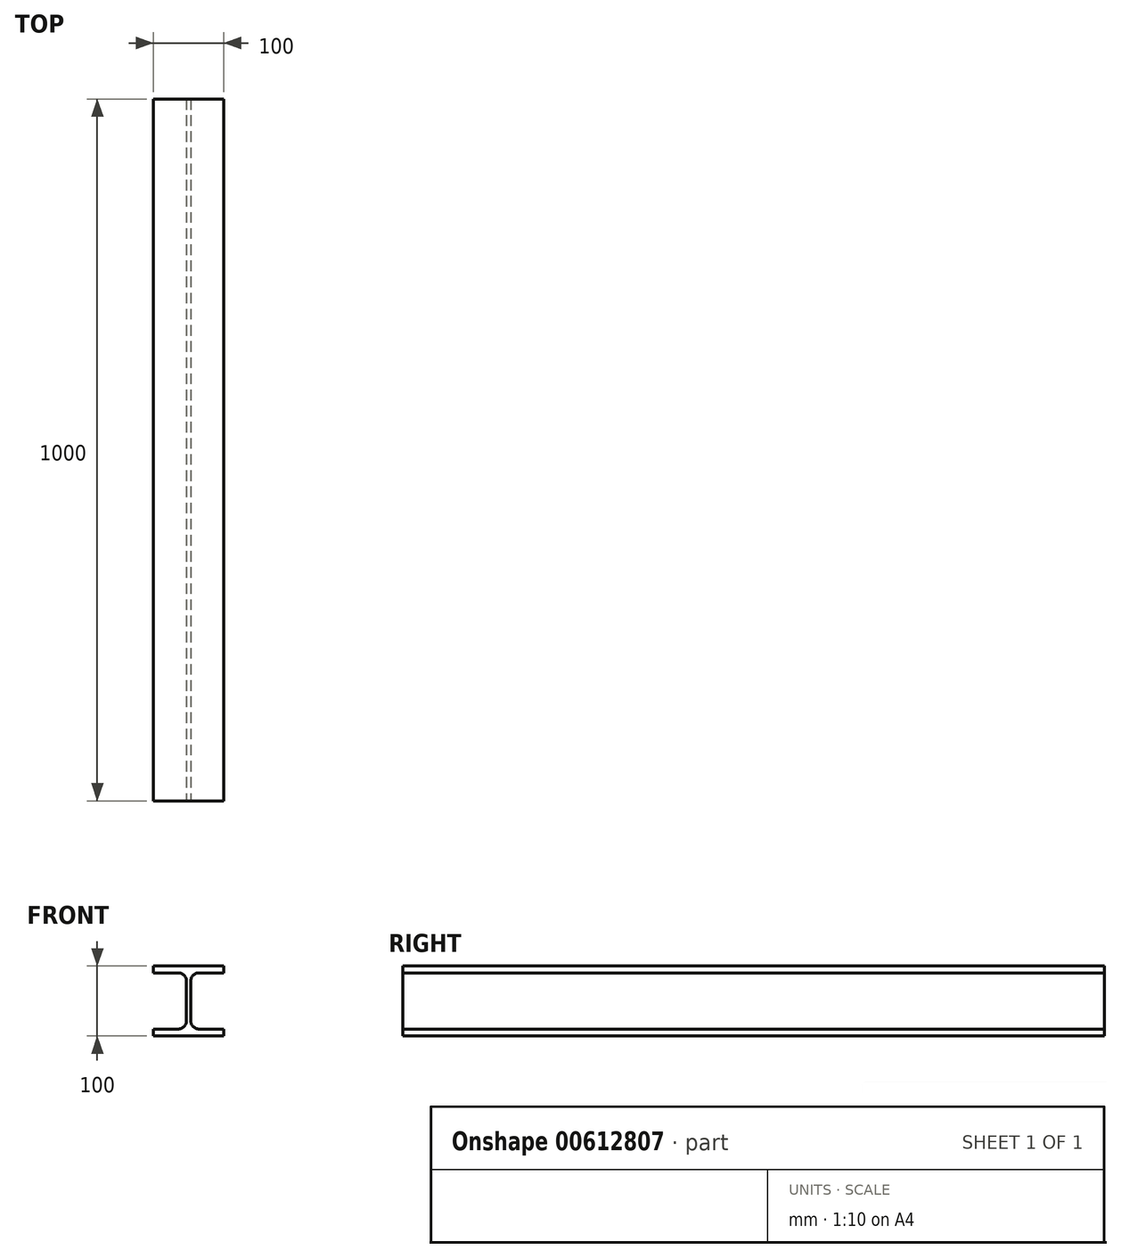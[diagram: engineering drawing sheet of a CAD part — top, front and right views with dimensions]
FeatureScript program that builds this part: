
annotation { "Feature Type Name" : "Feature", "Feature Type Description" : "" }
export const myFeature = defineFeature(function(context is Context, id is Id, definition is map)
    precondition{}
    {
        {
            var Q0;
            Q0=qCreatedBy(makeId("Front.planeOp"),FACE);
            var sketch = newSketch(context, id + "F0", { "sketchPlane" : qUnion([Q0])});
            skLineSegment(sketch, "E0.left", {"start": v(50, -40) * mm, "end": v(50, -50) * mm});
            skPoint(sketch, "E0.middle", {"position": v(0, 0) * mm});
            skLineSegment(sketch, "E1", {"start": v(3, 0) * mm, "end": v(3, -28) * mm});
            skLineSegment(sketch, "E2", {"start": v(50, -40) * mm, "end": v(15, -40) * mm});
            skPoint(sketch, "E3.newPointB", {"position": v(0, -40) * mm});
            skArc(sketch, "E3.filletArc", {"start": v(3, -28) * mm, "mid": v(6.51, -36.49) * mm, "end": v(15, -40) * mm});
            skPoint(sketch, "E0.bottom.start.orphan", {"position": v(50, 50) * mm});
            skPoint(sketch, "E0.right.start.orphan", {"position": v(-50, 50) * mm});
            skPoint(sketch, "E0.top.end.orphan", {"position": v(-50, -50) * mm});
            skLineSegment(sketch, "E4", {"start": v(50, -50) * mm, "end": v(0, -50) * mm});
            skLineSegment(sketch, "E5.MirrorCS", {"start": v(-3, 0) * mm, "end": v(-3, -28) * mm});
            skArc(sketch, "E6.MirrorCS", {"start": v(-3, -28) * mm, "mid": v(-6.51, -36.49) * mm, "end": v(-15, -40) * mm});
            skLineSegment(sketch, "E7.MirrorCS", {"start": v(-50, -40) * mm, "end": v(-15, -40) * mm});
            skLineSegment(sketch, "E8.MirrorCS", {"start": v(-50, -40) * mm, "end": v(-50, -50) * mm});
            skLineSegment(sketch, "E9.MirrorCS", {"start": v(-50, -50) * mm, "end": v(0, -50) * mm});
            skLineSegment(sketch, "E10.MirrorCS", {"start": v(-3, 0) * mm, "end": v(-3, 28) * mm});
            skLineSegment(sketch, "E11.MirrorCS", {"start": v(3, 0) * mm, "end": v(3, 28) * mm});
            skLineSegment(sketch, "E12.MirrorCS", {"start": v(50, 40) * mm, "end": v(15, 40) * mm});
            skArc(sketch, "E13.MirrorCS", {"start": v(3, 28) * mm, "mid": v(6.51, 36.49) * mm, "end": v(15, 40) * mm});
            skArc(sketch, "E14.MirrorCS", {"start": v(-3, 28) * mm, "mid": v(-6.51, 36.49) * mm, "end": v(-15, 40) * mm});
            skLineSegment(sketch, "E15.MirrorCS", {"start": v(-50, 40) * mm, "end": v(-15, 40) * mm});
            skLineSegment(sketch, "E16.MirrorCS", {"start": v(-50, 40) * mm, "end": v(-50, 50) * mm});
            skLineSegment(sketch, "E17.MirrorCS", {"start": v(-50, 50) * mm, "end": v(0, 50) * mm});
            skLineSegment(sketch, "E18.MirrorCS", {"start": v(50, 50) * mm, "end": v(0, 50) * mm});
            skLineSegment(sketch, "E19.MirrorCS", {"start": v(50, 40) * mm, "end": v(50, 50) * mm});
            skSolve(sketch);
        }
        {
            var Q0;
            Q0 = qSketchRegion(id + "F0", true);
            extrude(context, id + "F1", {"entities" : qUnion([Q0]), "oppositeDirection" : true, "depth" : 1000 * mm, "offsetDistance" : 25 * mm});
        }
    });
